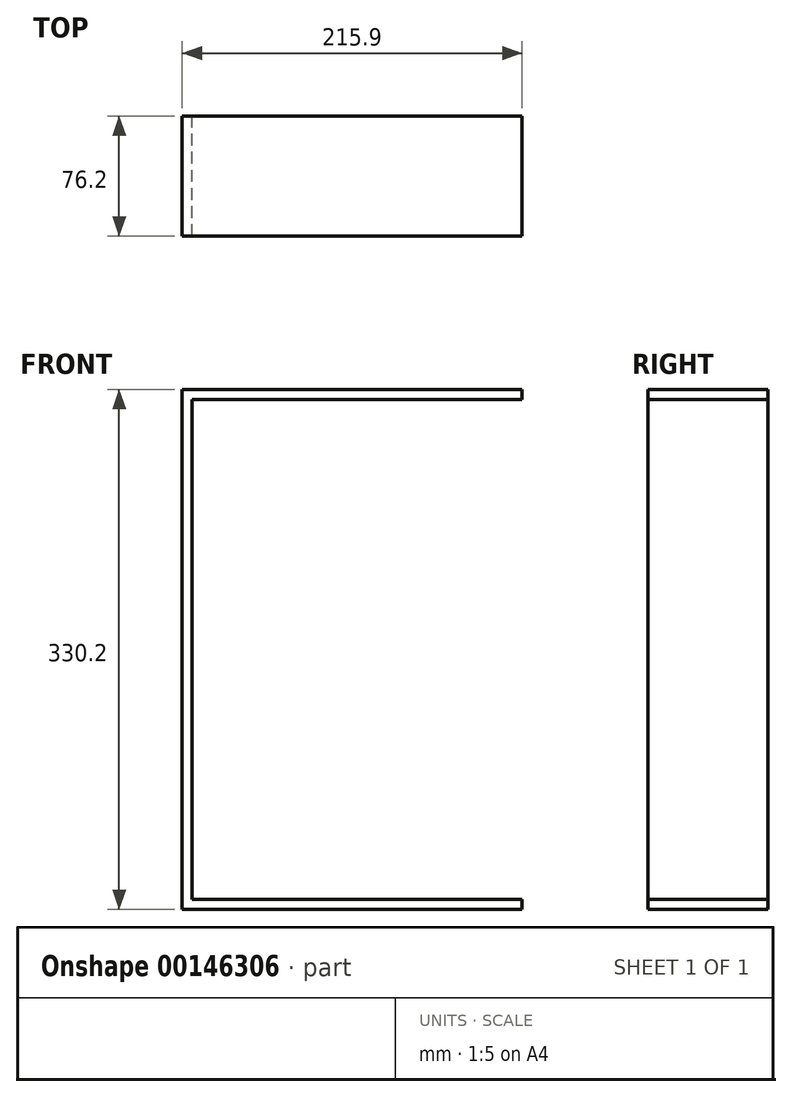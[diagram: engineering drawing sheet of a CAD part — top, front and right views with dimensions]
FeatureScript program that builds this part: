
annotation { "Feature Type Name" : "Feature", "Feature Type Description" : "" }
export const myFeature = defineFeature(function(context is Context, id is Id, definition is map)
    precondition{}
    {
        {
            var Q0;
            Q0=qCreatedBy(makeId("Front.planeOp"),FACE);
            var sketch = newSketch(context, id + "F0", { "sketchPlane" : qUnion([Q0])});
            skLineSegment(sketch, "E0", {"start": v(215.9, 0) * mm, "end": v(0, 0) * mm});
            skLineSegment(sketch, "E1", {"start": v(0, 0) * mm, "end": v(0, 330.2) * mm});
            skLineSegment(sketch, "E2", {"start": v(0, 330.2) * mm, "end": v(215.9, 330.2) * mm});
            skLineSegment(sketch, "E3", {"start": v(215.9, 330.2) * mm, "end": v(215.9, 323.85) * mm});
            skLineSegment(sketch, "E4", {"start": v(215.9, 323.85) * mm, "end": v(6.35, 323.85) * mm});
            skLineSegment(sketch, "E5", {"start": v(6.35, 323.85) * mm, "end": v(6.35, 6.35) * mm});
            skLineSegment(sketch, "E6", {"start": v(6.35, 6.35) * mm, "end": v(215.9, 6.35) * mm});
            skLineSegment(sketch, "E7", {"start": v(215.9, 6.35) * mm, "end": v(215.9, 0) * mm});
            skSolve(sketch);
        }
        {
            var Q0;
            Q0 = qSketchRegion(id + "F0", true);
            extrude(context, id + "F1", {"entities" : qUnion([Q0]), "depth" : 76.2 * mm});
        }
    });
